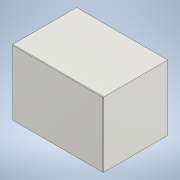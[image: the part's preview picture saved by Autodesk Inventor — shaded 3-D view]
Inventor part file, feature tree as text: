
AUTODESK INVENTOR PART (.ipt)
format: ipt  version: 2022 (Build 260153000, 153)  size: 118,272 bytes
history: native  units: mm
features: extrude x2, sketch x2, fillet x1
ambient origin geometry x8: Origin, YZ Plane, XZ Plane, XY Plane, X Axis, Y Axis, Z Axis, Center Point
bodies: Body1 (feature_tree)
feature tree (5):
  extrude  "Extrusão3"  Depth=254.0mm
  extrude  "Extrusão4"  Depth=2.0mm
  fillet  "Arredondamento1"  Radius=2.0mm
  sketch  "Esboço11"  dims[d14=354.0mm d15=254.0mm]
  sketch  "Esboço12"  dims[d16=2.0mm d17=2.0mm d18=2.0mm d19=2.0mm d20=250.0mm d21=0.0mm d22=2.0mm d23=0.0mm d24=2.0mm]
